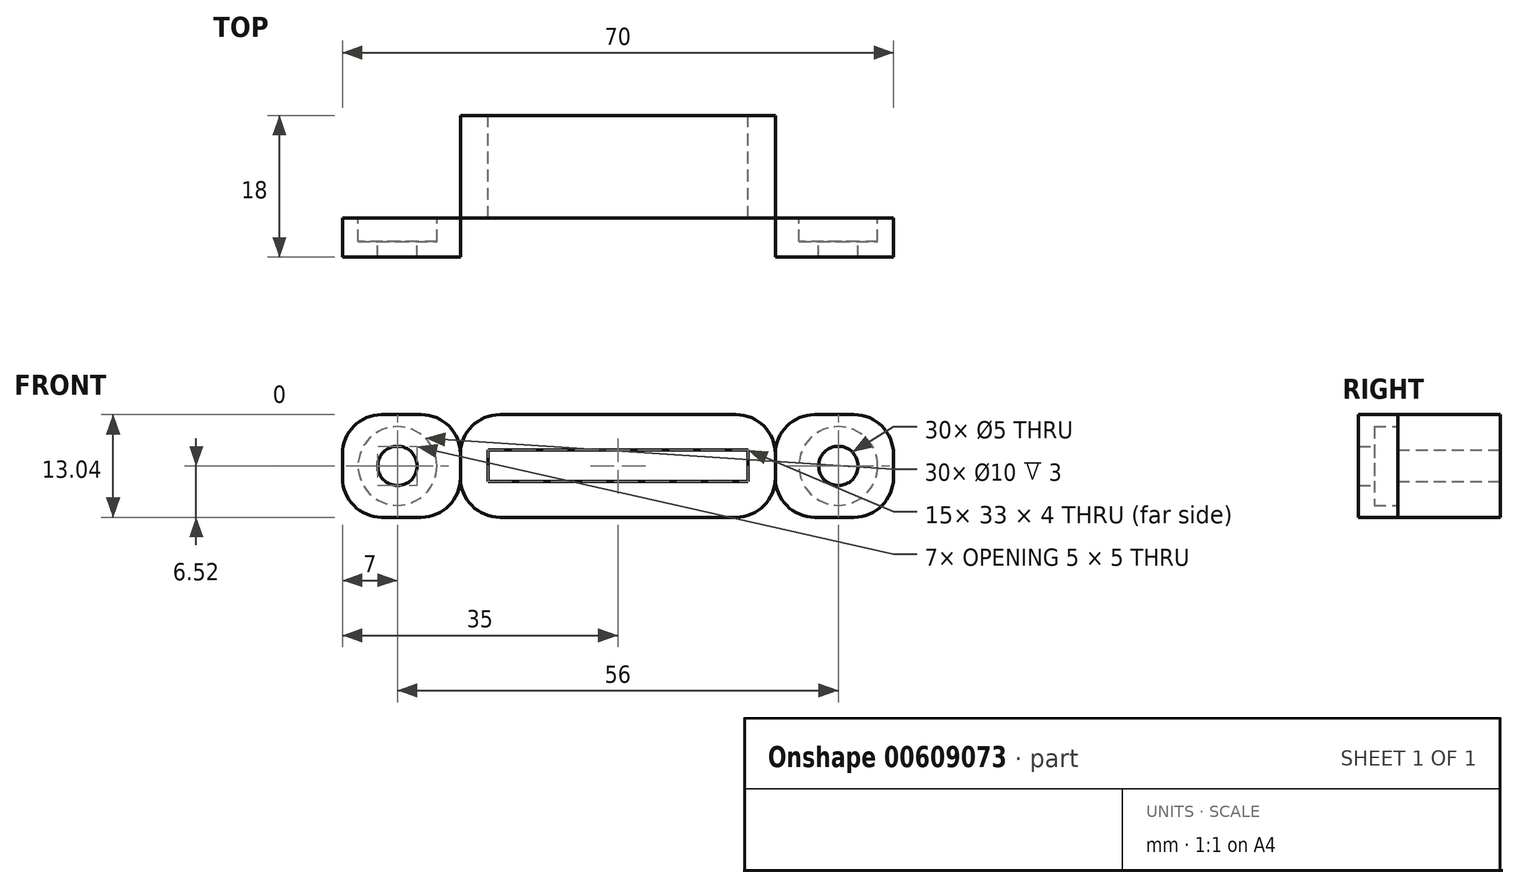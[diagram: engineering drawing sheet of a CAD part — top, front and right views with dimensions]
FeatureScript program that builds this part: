
annotation { "Feature Type Name" : "Feature", "Feature Type Description" : "" }
export const myFeature = defineFeature(function(context is Context, id is Id, definition is map)
    precondition{}
    {
        {
            var Q0;
            Q0=qCreatedBy(makeId("Top.planeOp"),FACE);
            var sketch = newSketch(context, id + "F0", { "sketchPlane" : qUnion([Q0])});
            skLineSegment(sketch, "E0.bottom", {"start": v(-16.5, 9) * mm, "end": v(16.5, 9) * mm});
            skLineSegment(sketch, "E0.top", {"start": v(-16.5, -9) * mm, "end": v(16.5, -9) * mm});
            skLineSegment(sketch, "E0.left", {"start": v(-16.5, 9) * mm, "end": v(-16.5, -9) * mm});
            skLineSegment(sketch, "E0.right", {"start": v(16.5, 9) * mm, "end": v(16.5, -9) * mm});
            skPoint(sketch, "E0.middle", {"position": v(0, 0) * mm});
            skLineSegment(sketch, "E1.bottom", {"start": v(-20, 9) * mm, "end": v(20, 9) * mm});
            skLineSegment(sketch, "E1.top", {"start": v(-20, -9) * mm, "end": v(20, -9) * mm});
            skLineSegment(sketch, "E1.left", {"start": v(-20, 9) * mm, "end": v(-20, -9) * mm});
            skLineSegment(sketch, "E1.right", {"start": v(20, 9) * mm, "end": v(20, -9) * mm});
            skLineSegment(sketch, "E2.top", {"start": v(-35, -4) * mm, "end": v(35, -4) * mm});
            skLineSegment(sketch, "E2.left", {"start": v(-35, -14) * mm, "end": v(-35, -4) * mm});
            skLineSegment(sketch, "E2.right", {"start": v(35, -14) * mm, "end": v(35, -4) * mm});
            skPoint(sketch, "E2.middle", {"position": v(0, -9) * mm});
            skLineSegment(sketch, "E3", {"start": v(0, -9) * mm, "end": v(-35, -9) * mm});
            skLineSegment(sketch, "E4", {"start": v(0, -9) * mm, "end": v(35, -9) * mm});
            skSolve(sketch);
        }
        {
            var Q0;
            {var subQ0=sQuery(id+"F0.wireOp",EDGE,"E1.bottom");var subQ1=sQuery(id+"F0.wireOp",EDGE,"E0.left");var subQ2=makeQuery(id+"F0.imprint","INTERSECT",VERTEX,{"derivedFrom":[subQ1,subQ0]});Q0=makeQuery(id+"F0.imprint","IMPRINT",FACE,{"disambiguationData":[TD([[makeQuery(id+"F0.imprint","IMPRINT",EDGE,{"disambiguationData":[TD([[subQ2,-1.0]])],"derivedFrom":subQ1}),1.0]])]});}
            var Q1;
            {var subQ0=sQuery(id+"F0.wireOp",EDGE,"E1.bottom");var subQ1=sQuery(id+"F0.wireOp",EDGE,"E0.left");var subQ2=makeQuery(id+"F0.imprint","INTERSECT",VERTEX,{"derivedFrom":[subQ1,subQ0]});Q1=makeQuery(id+"F0.imprint","IMPRINT",FACE,{"disambiguationData":[TD([[makeQuery(id+"F0.imprint","IMPRINT",EDGE,{"disambiguationData":[TD([[subQ2,-1.0]])],"derivedFrom":subQ1}),-1.0]])]});}
            var Q2;
            {var subQ0=sQuery(id+"F0.wireOp",EDGE,"E3");var subQ1=sQuery(id+"F0.wireOp",EDGE,"E0.left");var subQ2=makeQuery(id+"F0.imprint","INTERSECT",VERTEX,{"derivedFrom":[subQ1,subQ0]});Q2=makeQuery(id+"F0.imprint","IMPRINT",FACE,{"disambiguationData":[TD([[makeQuery(id+"F0.imprint","IMPRINT",EDGE,{"disambiguationData":[TD([[subQ2,1.0]])],"derivedFrom":subQ1}),1.0]])]});}
            var Q3;
            {var subQ0=sQuery(id+"F0.wireOp",EDGE,"E3");var subQ1=sQuery(id+"F0.wireOp",EDGE,"E0.left");var subQ2=makeQuery(id+"F0.imprint","INTERSECT",VERTEX,{"derivedFrom":[subQ1,subQ0]});Q3=makeQuery(id+"F0.imprint","IMPRINT",FACE,{"disambiguationData":[TD([[makeQuery(id+"F0.imprint","IMPRINT",EDGE,{"disambiguationData":[TD([[subQ2,1.0]])],"derivedFrom":subQ1}),-1.0]])]});}
            var Q4;
            {var subQ0=sQuery(id+"F0.wireOp",EDGE,"E3");var subQ1=sQuery(id+"F0.wireOp",EDGE,"E1.left");var subQ2=makeQuery(id+"F0.imprint","INTERSECT",VERTEX,{"derivedFrom":[subQ1,subQ0]});Q4=makeQuery(id+"F0.imprint","IMPRINT",FACE,{"disambiguationData":[TD([[makeQuery(id+"F0.imprint","IMPRINT",EDGE,{"disambiguationData":[TD([[subQ2,1.0]])],"derivedFrom":subQ1}),-1.0]])]});}
            var Q5;
            {var subQ0=sQuery(id+"F0.wireOp",EDGE,"E1.bottom");var subQ1=sQuery(id+"F0.wireOp",EDGE,"E0.right");var subQ2=makeQuery(id+"F0.imprint","INTERSECT",VERTEX,{"derivedFrom":[subQ1,subQ0]});Q5=makeQuery(id+"F0.imprint","IMPRINT",FACE,{"disambiguationData":[TD([[makeQuery(id+"F0.imprint","IMPRINT",EDGE,{"disambiguationData":[TD([[subQ2,-1.0]])],"derivedFrom":subQ1}),1.0]])]});}
            var Q6;
            {var subQ0=sQuery(id+"F0.wireOp",EDGE,"E4");var subQ1=sQuery(id+"F0.wireOp",EDGE,"E0.right");var subQ2=makeQuery(id+"F0.imprint","INTERSECT",VERTEX,{"derivedFrom":[subQ1,subQ0]});Q6=makeQuery(id+"F0.imprint","IMPRINT",FACE,{"disambiguationData":[TD([[makeQuery(id+"F0.imprint","IMPRINT",EDGE,{"disambiguationData":[TD([[subQ2,1.0]])],"derivedFrom":subQ1}),1.0]])]});}
            var Q7;
            {var subQ0=sQuery(id+"F0.wireOp",EDGE,"E4");var subQ1=sQuery(id+"F0.wireOp",EDGE,"E1.right");var subQ2=makeQuery(id+"F0.imprint","INTERSECT",VERTEX,{"derivedFrom":[subQ1,subQ0]});Q7=makeQuery(id+"F0.imprint","IMPRINT",FACE,{"disambiguationData":[TD([[makeQuery(id+"F0.imprint","IMPRINT",EDGE,{"disambiguationData":[TD([[subQ2,1.0]])],"derivedFrom":subQ1}),1.0]])]});}
            extrude(context, id + "F1", {"entities" : qUnion([Q0, Q1, Q2, Q3, Q4, Q5, Q6, Q7]), "depth" : 13.04 * mm, "offsetDistance" : 25 * mm});
        }
        {
            var Q0;
            Q0=makeQuery(id+"F1.opExtrude","SWEPT_FACE",FACE,{"disambiguationData":[OSD([sQuery(id+"F0.wireOp",EDGE,"E1.bottom")])]});
            var sketch = newSketch(context, id + "F2", { "sketchPlane" : qUnion([Q0])});
            skLineSegment(sketch, "E5.bottom", {"start": v(-16.5, 8.52) * mm, "end": v(16.5, 8.52) * mm});
            skLineSegment(sketch, "E5.top", {"start": v(-16.5, 4.52) * mm, "end": v(16.5, 4.52) * mm});
            skLineSegment(sketch, "E5.left", {"start": v(-16.5, 8.52) * mm, "end": v(-16.5, 4.52) * mm});
            skLineSegment(sketch, "E5.right", {"start": v(16.5, 8.52) * mm, "end": v(16.5, 4.52) * mm});
            skSolve(sketch);
        }
        {
            var Q0;
            Q0=makeQuery(id+"F2.imprint","IMPRINT",FACE,{"disambiguationData":[TD([[makeQuery(id+"F2.imprint","IMPRINT",EDGE,{"derivedFrom":sQuery(id+"F2.wireOp",EDGE,"E5.bottom")}),-1.0]])]});
            extrude(context, id + "F3", {"entities" : qUnion([Q0]), "operationType" : NewBodyOperationType.REMOVE, "oppositeDirection" : true, "depth" : 40.6 * mm, "offsetDistance" : 25 * mm});
        }
        {
            var Q0;
            {var subQ0=sQuery(id+"F0.wireOp",EDGE,"E2.top");Q0=makeQuery(id+"F1.opExtrude","SWEPT_FACE",FACE,{"disambiguationData":[OSD([subQ0]),TDD([makeQuery(id+"F0.imprint","IMPRINT",EDGE,{"disambiguationData":[TD([[makeQuery(id+"F0.imprint","INTERSECT",VERTEX,{"derivedFrom":[subQ0,sQuery(id+"F0.wireOp",EDGE,"E2.right")]}),1.0]])],"derivedFrom":subQ0})])]});}
            var sketch = newSketch(context, id + "F4", { "sketchPlane" : qUnion([Q0])});
            skCircle(sketch, "E6", {"center": v(-28, 6.52) * mm, "radius": 2.5 * mm});
            skCircle(sketch, "E7", {"center": v(-28, 6.52) * mm, "radius": 5 * mm});
            skSolve(sketch);
        }
        {
            var Q0;
            {var subQ0=sQuery(id+"F0.wireOp",EDGE,"E2.top");Q0=makeQuery(id+"F1.opExtrude","SWEPT_FACE",FACE,{"disambiguationData":[OSD([subQ0]),TDD([makeQuery(id+"F0.imprint","IMPRINT",EDGE,{"disambiguationData":[TD([[makeQuery(id+"F0.imprint","INTERSECT",VERTEX,{"derivedFrom":[subQ0,sQuery(id+"F0.wireOp",EDGE,"E2.left")]}),-1.0]])],"derivedFrom":subQ0})])]});}
            var sketch = newSketch(context, id + "F5", { "sketchPlane" : qUnion([Q0])});
            skCircle(sketch, "E8", {"center": v(28, 6.52) * mm, "radius": 2.5 * mm});
            skCircle(sketch, "E9", {"center": v(28, 6.52) * mm, "radius": 5 * mm});
            skSolve(sketch);
        }
        {
            var Q0;
            Q0=makeQuery(id+"F4.imprint","IMPRINT",FACE,{"disambiguationData":[TD([[makeQuery(id+"F4.imprint","IMPRINT",EDGE,{"derivedFrom":sQuery(id+"F4.wireOp",EDGE,"E6")}),1.0]])]});
            var Q1;
            Q1=makeQuery(id+"F5.imprint","IMPRINT",FACE,{"disambiguationData":[TD([[makeQuery(id+"F5.imprint","IMPRINT",EDGE,{"derivedFrom":sQuery(id+"F5.wireOp",EDGE,"E8")}),1.0]])]});
            extrude(context, id + "F6", {"entities" : qUnion([Q0, Q1]), "operationType" : NewBodyOperationType.REMOVE, "oppositeDirection" : true, "depth" : 9.9 * mm, "offsetDistance" : 25 * mm});
        }
        {
            var Q0;
            Q0=makeQuery(id+"F4.imprint","IMPRINT",FACE,{"disambiguationData":[TD([[makeQuery(id+"F4.imprint","IMPRINT",EDGE,{"derivedFrom":sQuery(id+"F4.wireOp",EDGE,"E6")}),-1.0]])]});
            var Q1;
            Q1=makeQuery(id+"F5.imprint","IMPRINT",FACE,{"disambiguationData":[TD([[makeQuery(id+"F5.imprint","IMPRINT",EDGE,{"derivedFrom":sQuery(id+"F5.wireOp",EDGE,"E8")}),-1.0]])]});
            extrude(context, id + "F7", {"entities" : qUnion([Q0, Q1]), "operationType" : NewBodyOperationType.REMOVE, "oppositeDirection" : true, "depth" : 3 * mm, "offsetDistance" : 25 * mm});
        }
        {
            var Q0;
            Q0=makeQuery(id+"F1.opExtrude","CAP_EDGE",EDGE,{"disambiguationData":[OSD([sQuery(id+"F0.wireOp",EDGE,"E2.right")])],"isStart":false});
            var Q1;
            Q1=makeQuery(id+"F1.opExtrude","CAP_EDGE",EDGE,{"disambiguationData":[OSD([sQuery(id+"F0.wireOp",EDGE,"E2.right")])],"isStart":true});
            var Q2;
            Q2=makeQuery(id+"F1.opExtrude","CAP_EDGE",EDGE,{"disambiguationData":[OSD([sQuery(id+"F0.wireOp",EDGE,"E2.left")])],"isStart":false});
            var Q3;
            Q3=makeQuery(id+"F1.opExtrude","CAP_EDGE",EDGE,{"disambiguationData":[OSD([sQuery(id+"F0.wireOp",EDGE,"E2.left")])],"isStart":true});
            var Q4;
            Q4=makeQuery(id+"F1.opExtrude","CAP_EDGE",EDGE,{"disambiguationData":[OSD([sQuery(id+"F0.wireOp",EDGE,"E1.right")])],"isStart":false});
            var Q5;
            Q5=makeQuery(id+"F1.opExtrude","CAP_EDGE",EDGE,{"disambiguationData":[OSD([sQuery(id+"F0.wireOp",EDGE,"E1.left")])],"isStart":false});
            var Q6;
            Q6=makeQuery(id+"F1.opExtrude","CAP_EDGE",EDGE,{"disambiguationData":[OSD([sQuery(id+"F0.wireOp",EDGE,"E1.left")])],"isStart":true});
            var Q7;
            Q7=makeQuery(id+"F1.opExtrude","CAP_EDGE",EDGE,{"disambiguationData":[OSD([sQuery(id+"F0.wireOp",EDGE,"E1.right")])],"isStart":true});
            fillet(context, id + "F8", {"entities" : qUnion([Q0, Q1, Q2, Q3, Q4, Q5, Q6, Q7]), "radius" : 5 * mm, "tangentPropagation" : true, "allowEdgeOverflow" : false});
        }
    });
